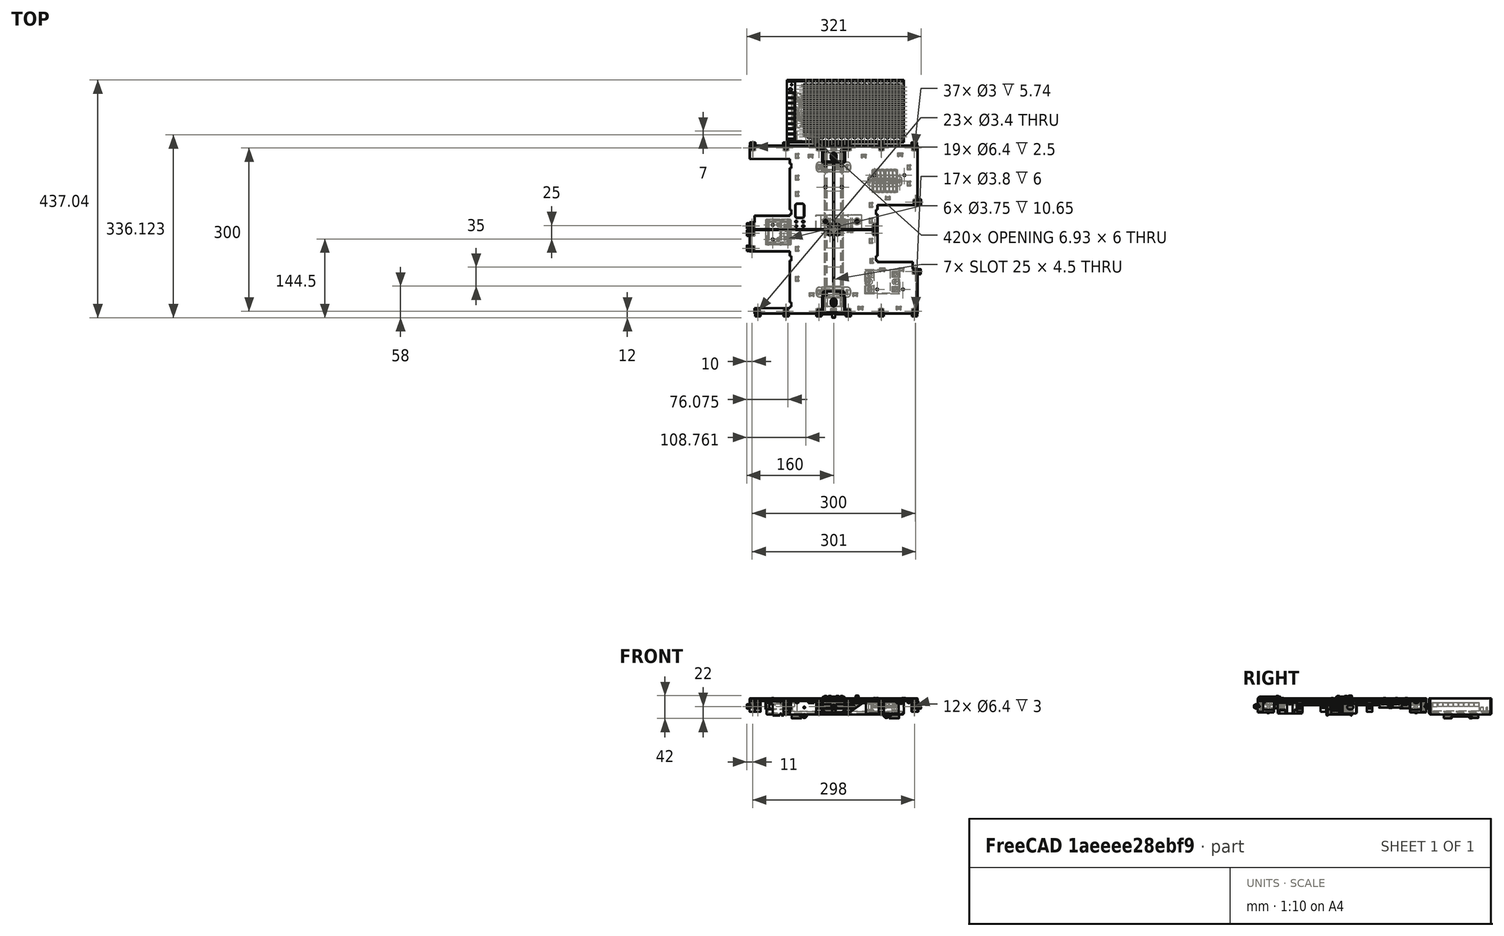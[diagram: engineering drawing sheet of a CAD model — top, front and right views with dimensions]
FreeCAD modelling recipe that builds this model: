
FCSTD DOCUMENT  (FreeCAD 0.19R24291 (Git))
Label: bottom-panel-assembly
License: Other
LicenseURL: GPL3
objects: Part::FeaturePython×86, Part::Feature×43, App::Part×10, PartDesign::CoordinateSystem×1
note: 130 computed .brp shape members not serialized (recipe doc carries the construction recipe); baked Part::Feature solids carry a one-line shape summary decoded from their .brp

FEATURE [Part::Feature] Cut002015026005020007004001  label="center-panel-connector"
  Placement = pos=(0,0,30) rot=(0,0,1;0rad)
  shape: bbox 22 x 22 x 3 mm, 24 faces (baked)
FEATURE [Part::FeaturePython] Screw013  label="M3x6-Screw"  # Fasteners workbench fastener (typed FeaturePython)
  Placement = pos=(-7,-7,33) rot=(0,0,1;0rad)
  baseObject = -> Cut002015026005020007004001 [Edge41]
  diameter = 1
  invert = false
  length = 0
  lengthCustom = 6
  matchOuter = true
  offset = 0
  thread = false
  type = 40
FEATURE [Part::FeaturePython] Screw014  label="M3x6-Screw014"  # Fasteners workbench fastener (typed FeaturePython)
  Placement = pos=(-7,7,33) rot=(0,0,1;0rad)
  baseObject = -> Cut002015026005020007004001 [Edge42]
  diameter = 1
  invert = false
  length = 0
  lengthCustom = 6
  matchOuter = true
  offset = 0
  thread = false
  type = 40
FEATURE [Part::FeaturePython] Screw015  label="M3x6-Screw015"  # Fasteners workbench fastener (typed FeaturePython)
  Placement = pos=(7,7,33) rot=(0,0,1;0rad)
  baseObject = -> Cut002015026005020007004001 [Edge40]
  diameter = 1
  invert = false
  length = 0
  lengthCustom = 6
  matchOuter = true
  offset = 0
  thread = false
  type = 40
FEATURE [Part::FeaturePython] Screw016  label="M3x6-Screw016"  # Fasteners workbench fastener (typed FeaturePython)
  Placement = pos=(7,-7,33) rot=(0,0,1;0rad)
  baseObject = -> Cut002015026005020007004001 [Edge39]
  diameter = 1
  invert = false
  length = 0
  lengthCustom = 6
  matchOuter = true
  offset = 0
  thread = false
  type = 40
FEATURE [Part::Feature] Cut001001  label="front-din-cap"
  Placement = pos=(0,-140,25) rot=(0,0,1;0rad)
  shape: bbox 40 x 41.5 x 9 mm, 50 faces (baked)
FEATURE [Part::Feature] Chamfer003004002  label="bottom-din-holder"
  Placement = pos=(-3.4e-14,-140,0) rot=(0,0,1;3.14159rad)
  shape: bbox 40 x 31 x 21 mm, 75 faces (baked)
FEATURE [Part::Feature] Chamfer005007002029002004001  label="back-din-cap"
  Placement = pos=(0,140,0) rot=(0,0,1;0rad)
  shape: bbox 40 x 30 x 6 mm, 55 faces (baked)
FEATURE [Part::Feature] Chamfer003001001  label="bottom-din-holder001"
  Placement = pos=(0,140,0) rot=(0,0,1;0rad)
  shape: bbox 40 x 31 x 21 mm, 75 faces (baked)
FEATURE [Part::Feature] Common001001  label="din-282mm001"
  Placement = pos=(-5e-15,0.5,24.5) rot=(0.707107,0.707107,0;3.14159rad)
  shape: bbox 35 x 282 x 7.5 mm, 66 faces (baked)
FEATURE [Part::FeaturePython] Nut  label="M4-Nut"  # Fasteners workbench fastener (typed FeaturePython)
  Placement = pos=(0,136,7) rot=(1,0,0;3.14159rad)
  baseObject = -> Chamfer003001001 [Edge141]
  diameter = 6
  invert = true
  matchOuter = true
  offset = 0
  thread = false
  type = 7
FEATURE [Part::FeaturePython] Nut001  label="M4-Nut001"  # Fasteners workbench fastener (typed FeaturePython)
  Placement = pos=(-3.4e-14,-136,7) rot=(1,0,0;3.14159rad)
  baseObject = -> Chamfer003004002 [Edge141]
  diameter = 6
  invert = true
  matchOuter = true
  offset = 0
  thread = false
  type = 7
FEATURE [Part::FeaturePython] HeatSet034  label="M3x4-HeatSet026"  # WARN: FeaturePython — macro-defined, semantics opaque (R4)
  Placement = pos=(-15,145,30) rot=(0,0,1;0rad)
  baseObject = -> Chamfer005007002029002004001 [Edge88]
  diameter = 2
  invert = false
  offset = 0
FEATURE [Part::FeaturePython] HeatSet035  label="M3x4-HeatSet027"  # WARN: FeaturePython — macro-defined, semantics opaque (R4)
  Placement = pos=(15,145,30) rot=(0,0,1;0rad)
  baseObject = -> Chamfer005007002029002004001 [Edge114]
  diameter = 2
  invert = false
  offset = 0
FEATURE [Part::FeaturePython] Screw034  label="M3x6-Screw019"  # Fasteners workbench fastener (typed FeaturePython)
  Placement = pos=(15,-119,33) rot=(0,0,1;0rad)
  baseObject = -> Cut001001 [Edge45]
  diameter = 1
  invert = false
  length = 0
  lengthCustom = 6
  matchOuter = true
  offset = 0
  thread = false
  type = 40
FEATURE [Part::FeaturePython] Screw035  label="M3x6-Screw020"  # Fasteners workbench fastener (typed FeaturePython)
  Placement = pos=(-15,-119,33) rot=(0,0,1;0rad)
  baseObject = -> Cut001001 [Edge44]
  diameter = 1
  invert = false
  length = 0
  lengthCustom = 6
  matchOuter = true
  offset = 0
  thread = false
  type = 40
FEATURE [Part::FeaturePython] Screw038  label="M6x12-Screw"  # Fasteners workbench fastener (typed FeaturePython)
  Placement = pos=(-3.4e-14,-150,15) rot=(-1,0,0;1.5708rad)
  baseObject = -> Chamfer003004002 [Edge49]
  diameter = 4
  invert = true
  length = 1
  lengthCustom = 12
  matchOuter = true
  offset = 0
  thread = false
  type = 40
FEATURE [Part::FeaturePython] Screw039  label="M6x12-Screw001"  # Fasteners workbench fastener (typed FeaturePython)
  Placement = pos=(0,150,15) rot=(1,0,0;1.5708rad)
  baseObject = -> Chamfer003001001 [Edge49]
  diameter = 4
  invert = true
  length = 1
  lengthCustom = 12
  matchOuter = true
  offset = 0
  thread = false
  type = 40
FEATURE [Part::FeaturePython] Screw040  label="M4x25-Screw"  # Fasteners workbench fastener (typed FeaturePython)
  Placement = pos=(2.6e-14,136,27.5) rot=(0,0,1;0rad)
  baseObject = -> Chamfer005007002029002004001 [Edge49]
  diameter = 2
  invert = false
  length = 7
  lengthCustom = 25
  matchOuter = true
  offset = 0
  thread = false
  type = 40
FEATURE [Part::FeaturePython] Screw041  label="M4x25-Screw001"  # Fasteners workbench fastener (typed FeaturePython)
  Placement = pos=(-3.4e-14,-136,27.5) rot=(0,0,1;0rad)
  baseObject = -> Cut001001 [Edge118]
  diameter = 2
  invert = false
  length = 7
  lengthCustom = 25
  matchOuter = true
  offset = 0
  thread = false
  type = 40
FEATURE [App::Part] Part002  label="din-mounter"
  Group = -> [Cut001001,Chamfer003004002,Chamfer005007002029002004001,Chamfer003001001,Common001001,Nut001,Nut,HeatSet034,HeatSet035,Screw034,Screw035,Screw038,Screw039,Screw040,Screw041]
  Origin = -> Origin002
FEATURE [Part::Feature] Cut002001001  label="sonoff-mount"
  Placement = pos=(-102,-4.75,24.5) rot=(0.707107,-0.707107,0;3.14159rad)
  shape: bbox 47 x 47 x 26.5 mm, 108 faces (baked)
FEATURE [Part::Feature] Fusion006002011004053036004001028003005004  label="SonOff-mini"
  Placement = pos=(-102,-5,10) rot=(0.57735,-0.57735,0.57735;4.18879rad)
  shape: bbox 43.4 x 42.65 x 19.85 mm, 152 faces (baked)
FEATURE [Part::Feature] Cut009001  label="wago-mount"
  Placement = pos=(95,89,24.5) rot=(0.707107,0.707107,0;3.14159rad)
  shape: bbox 63.6 x 41.99 x 12.2 mm, 224 faces (baked)
FEATURE [Part::Feature] Part__Feature001  label="WAGO 222-3c-002"
  Placement = pos=(71.5,89.5,22.5) rot=(0.57735,-0.57735,0.57735;4.18879rad)
  shape: bbox 22.7 x 21.3 x 9.8 mm, 151 faces (baked)
FEATURE [Part::Feature] Part__Feature003  label="WAGO 222-3c-004"
  Placement = pos=(94.2,89.5,22.5) rot=(0.57735,0.57735,-0.57735;4.18879rad)
  shape: bbox 22.7 x 21.3 x 9.8 mm, 151 faces (baked)
FEATURE [Part::Feature] Part__Feature002  label="WAGO 222-3c-003"
  Placement = pos=(116.7,89.5,22.5) rot=(0.57735,0.57735,-0.57735;4.18879rad)
  shape: bbox 22.7 x 21.3 x 9.8 mm, 151 faces (baked)
FEATURE [Part::Feature] Part__Feature  label="WAGO 222-3c-001"
  Placement = pos=(94,89.5,22.5) rot=(0.57735,-0.57735,0.57735;4.18879rad)
  shape: bbox 22.7 x 21.3 x 9.8 mm, 151 faces (baked)
FEATURE [Part::Feature] Fusion006002011004053036004001028003005005  label="SSR0omron"
  Placement = pos=(89,-96,2.5) rot=(0.57735,-0.57735,0.57735;4.18879rad)
  shape: bbox 64 x 45 x 22.5 mm, 84 faces (baked)
FEATURE [Part::FeaturePython] Screw042  label="M3x6-Screw021"  # Fasteners workbench fastener (typed FeaturePython)
  Placement = pos=(-102,-19,21.5) rot=(1,0,0;3.14159rad)
  baseObject = -> Cut002001001 [Edge319]
  diameter = 1
  invert = false
  length = 0
  lengthCustom = 6
  matchOuter = true
  offset = 0
  thread = false
  type = 40
FEATURE [Part::FeaturePython] Screw043  label="M3x6-Screw022"  # Fasteners workbench fastener (typed FeaturePython)
  Placement = pos=(-102,8.5,21.5) rot=(1,0,0;3.14159rad)
  baseObject = -> Cut002001001 [Edge316]
  diameter = 1
  invert = false
  length = 0
  lengthCustom = 6
  matchOuter = true
  offset = 0
  thread = false
  type = 40
FEATURE [App::Part] Part003  label="sonoff-switch"
  Group = -> [Fusion006002011004053036004001028003005004,Cut002001001,Screw042,Screw043]
  Origin = -> Origin003
  Placement = pos=(-10,0,0) rot=(0,0,1;0rad)
FEATURE [Part::FeaturePython] Screw044  label="M3x6-Screw024"  # Fasteners workbench fastener (typed FeaturePython)
  Placement = pos=(66.5,89,21.5) rot=(1,0,0;3.14159rad)
  baseObject = -> Cut009001 [Edge435]
  diameter = 1
  invert = false
  length = 0
  lengthCustom = 6
  matchOuter = true
  offset = 0
  thread = false
  type = 40
FEATURE [Part::FeaturePython] Screw045  label="M3x6-Screw023"  # Fasteners workbench fastener (typed FeaturePython)
  Placement = pos=(121.5,89,21.5) rot=(1,0,0;3.14159rad)
  baseObject = -> Cut009001 [Edge192]
  diameter = 1
  invert = false
  length = 0
  lengthCustom = 6
  matchOuter = true
  offset = 0
  thread = false
  type = 40
FEATURE [App::Part] Part004  label="wago-connectors"
  Group = -> [Screw045,Screw044,Part__Feature001,Part__Feature003,Part__Feature002,Part__Feature,Cut009001]
  Origin = -> Origin004
  Placement = pos=(8.5,11,0) rot=(0,0,1;0rad)
FEATURE [Part::FeaturePython] Washer001  label="M3-Washer"  # Fasteners workbench fastener (typed FeaturePython)
  Placement = pos=(113.418,-96,21.5) rot=(1,0,0;3.14159rad)
  baseObject = -> Fusion006002011004053036004001028003005005 [Edge76]
  diameter = 4
  invert = false
  matchOuter = true
  offset = 0
  type = 5
FEATURE [Part::FeaturePython] Washer  label="M3-Washer001"  # Fasteners workbench fastener (typed FeaturePython)
  Placement = pos=(65.4176,-96,21.5) rot=(1,0,0;3.14159rad)
  baseObject = -> Fusion006002011004053036004001028003005005 [Edge152]
  diameter = 4
  invert = false
  matchOuter = true
  offset = 0
  type = 5
FEATURE [Part::FeaturePython] Screw046  label="M3x6-Screw025"  # Fasteners workbench fastener (typed FeaturePython)
  Placement = pos=(65.4176,-96,20.95) rot=(1,0,0;3.14159rad)
  baseObject = -> Washer [Edge1]
  diameter = 1
  invert = false
  length = 0
  lengthCustom = 6
  matchOuter = true
  offset = 0
  thread = false
  type = 40
FEATURE [Part::FeaturePython] Screw047  label="M3x6-Screw026"  # Fasteners workbench fastener (typed FeaturePython)
  Placement = pos=(113.418,-96,20.95) rot=(1,0,0;3.14159rad)
  baseObject = -> Washer001 [Edge1]
  diameter = 1
  invert = false
  length = 0
  lengthCustom = 6
  matchOuter = true
  offset = 0
  thread = false
  type = 40
FEATURE [App::Part] Part005  label="ssr"
  Group = -> [Washer001,Washer,Screw046,Screw047,Fusion006002011004053036004001028003005005]
  Origin = -> Origin005
  Placement = pos=(14.5,-14,0) rot=(0,0,1;0rad)
FEATURE [Part::Feature] Fusion006002011004053036004001028003005014018035002002  label="lrs-psu"
  Placement = pos=(0,-5,0) rot=(0,0,1;0rad)
  shape: bbox 215 x 115 x 30.01 mm, 2625 faces, 2 solids (baked)
FEATURE [PartDesign::CoordinateSystem] LCS_bottom_panel_assembly  label="LCS_bottom-panel-assembly"
  AttacherType = Attacher::AttachEngine3D
FEATURE [Part::Feature] Cut026001  label="din-wire-mounter"
  Placement = pos=(-0.5,115,23.5) rot=(0.707107,0.707107,0;3.14159rad)
  shape: bbox 63.6 x 18 x 7.6 mm, 203 faces (baked)
FEATURE [Part::Feature] Cut002015026005020007014007002001002  label="din-wire-mounter001"
  Placement = pos=(-0.5,-115,23.5) rot=(0.707107,0.707107,0;3.14159rad)
  shape: bbox 63.6 x 18 x 7.6 mm, 203 faces (baked)
FEATURE [App::Part] Part008  label="extra-cable-mounter"
  Group = -> [Cut026001,Cut002015026005020007014007002001002]
  Origin = -> Origin008
FEATURE [Part::Feature] Part__Feature112001118  label="IEC Screw Mount Plug Socket Male"
  Placement = pos=(13,3e-15,14) rot=(0,0.707107,-0.707107;3.14159rad)
  shape: bbox 51.91 x 24.6 x 22.99 mm, 108 faces (baked)
FEATURE [Part::FeaturePython] Screw056  label="M6x25-Screw"  # Fasteners workbench fastener (typed FeaturePython)
  Placement = pos=(-15,15,8) rot=(1,0,0;3.14159rad)
  diameter = 4
  invert = true
  length = 5
  lengthCustom = 25
  matchOuter = true
  offset = 0
  thread = false
  type = 40
FEATURE [Part::FeaturePython] Screw057  label="M6x14-Screw"  # Fasteners workbench fastener (typed FeaturePython)
  Placement = pos=(43,15,21) rot=(1,0,0;3.14159rad)
  diameter = 4
  invert = true
  length = 2
  lengthCustom = 14
  matchOuter = true
  offset = 0
  thread = false
  type = 40
FEATURE [Part::FeaturePython] HeatSet040  label="M3x4-HeatSet033"  # WARN: FeaturePython — macro-defined, semantics opaque (R4)
  Placement = pos=(-7,4e-15,14) rot=(1,0,0;1.5708rad)
  diameter = 2
  invert = true
  offset = 0
FEATURE [Part::FeaturePython] HeatSet041  label="M3x4-HeatSet032"  # WARN: FeaturePython — macro-defined, semantics opaque (R4)
  Placement = pos=(33,4e-15,14) rot=(1,0,0;1.5708rad)
  diameter = 2
  invert = true
  offset = 0
FEATURE [Part::FeaturePython] Screw058  label="M3x10-Screw036"  # Fasteners workbench fastener (typed FeaturePython)
  Placement = pos=(-7,-2.5,14) rot=(1,0,0;1.5708rad)
  baseObject = -> Part__Feature112001118 [Edge8]
  diameter = 4
  invert = false
  length = 3
  lengthCustom = 10
  matchOuter = true
  offset = 1
  thread = false
  type = 34
FEATURE [Part::FeaturePython] Screw059  label="M3x10-Screw035"  # Fasteners workbench fastener (typed FeaturePython)
  Placement = pos=(33,-2.5,14) rot=(1,0,0;1.5708rad)
  baseObject = -> Part__Feature112001118 [Edge12]
  diameter = 4
  invert = false
  length = 3
  lengthCustom = 10
  matchOuter = true
  offset = 1
  thread = false
  type = 34
FEATURE [Part::Feature] Chamfer005007002028001  label="panel-FR"
  Placement = pos=(0,0,25) rot=(0,0,1;0rad)
  shape: bbox 154 x 154 x 9 mm, 176 faces (baked)
FEATURE [Part::Feature] Chamfer005007002028002  label="panel-BR"
  Placement = pos=(0,0,25) rot=(0,0,1;0rad)
  shape: bbox 154 x 154 x 9 mm, 173 faces (baked)
FEATURE [Part::Feature] Chamfer005007002027001  label="panel-FL"
  Placement = pos=(0,0,25) rot=(0,0,1;0rad)
  shape: bbox 154 x 154 x 9 mm, 125 faces (baked)
FEATURE [Part::FeaturePython] HeatSet  label="M3x4-HeatSet"  # WARN: FeaturePython — macro-defined, semantics opaque (R4)
  Placement = pos=(15,118,25) rot=(1,0,0;3.14159rad)
  baseObject = -> Chamfer005007002028002 [Edge77]
  diameter = 2
  invert = true
  offset = 0
FEATURE [Part::Feature] Chamfer005007002030001  label="panel-BL"
  Placement = pos=(0,0,25) rot=(0,0,1;0rad)
  shape: bbox 154 x 154 x 9 mm, 202 faces (baked)
FEATURE [Part::FeaturePython] HeatSet042  label="M3x4-HeatSet034"  # WARN: FeaturePython — macro-defined, semantics opaque (R4)
  Placement = pos=(-15,118,25) rot=(1,0,0;3.14159rad)
  baseObject = -> Chamfer005007002030001 [Edge68]
  diameter = 2
  invert = true
  offset = 0
FEATURE [Part::FeaturePython] HeatSet043  label="M3x4-HeatSet035"  # WARN: FeaturePython — macro-defined, semantics opaque (R4)
  Placement = pos=(-15,78,25) rot=(1,0,0;3.14159rad)
  baseObject = -> Chamfer005007002030001 [Edge67]
  diameter = 2
  invert = true
  offset = 0
FEATURE [Part::FeaturePython] HeatSet044  label="M3x4-HeatSet036"  # WARN: FeaturePython — macro-defined, semantics opaque (R4)
  Placement = pos=(-7,7,25) rot=(1,0,0;3.14159rad)
  baseObject = -> Chamfer005007002030001 [Edge66]
  diameter = 2
  invert = true
  offset = 0
FEATURE [Part::FeaturePython] HeatSet045  label="M3x4-HeatSet037"  # WARN: FeaturePython — macro-defined, semantics opaque (R4)
  Placement = pos=(15,78,25) rot=(1,0,0;3.14159rad)
  baseObject = -> Chamfer005007002028002 [Edge75]
  diameter = 2
  invert = true
  offset = 0
FEATURE [Part::FeaturePython] HeatSet046  label="M3x4-HeatSet038"  # WARN: FeaturePython — macro-defined, semantics opaque (R4)
  Placement = pos=(7,7,25) rot=(1,0,0;3.14159rad)
  baseObject = -> Chamfer005007002028002 [Edge74]
  diameter = 2
  invert = true
  offset = 0
FEATURE [Part::FeaturePython] HeatSet047  label="M3x4-HeatSet039"  # WARN: FeaturePython — macro-defined, semantics opaque (R4)
  Placement = pos=(-7,-7,25) rot=(1,0,0;3.14159rad)
  baseObject = -> Chamfer005007002027001 [Edge170]
  diameter = 2
  invert = true
  offset = 0
FEATURE [Part::FeaturePython] HeatSet048  label="M3x4-HeatSet040"  # WARN: FeaturePython — macro-defined, semantics opaque (R4)
  Placement = pos=(-15,-119,25) rot=(1,0,0;3.14159rad)
  baseObject = -> Chamfer005007002027001 [Edge168]
  diameter = 2
  invert = true
  offset = 0
FEATURE [Part::FeaturePython] HeatSet049  label="M3x4-HeatSet041"  # WARN: FeaturePython — macro-defined, semantics opaque (R4)
  Placement = pos=(7,-7,25) rot=(1,0,0;3.14159rad)
  baseObject = -> Chamfer005007002028001 [Edge79]
  diameter = 2
  invert = true
  offset = 0
FEATURE [Part::FeaturePython] HeatSet050  label="M3x4-HeatSet042"  # WARN: FeaturePython — macro-defined, semantics opaque (R4)
  Placement = pos=(15,-119,25) rot=(1,0,0;3.14159rad)
  baseObject = -> Chamfer005007002028001 [Edge76]
  diameter = 2
  invert = true
  offset = 0
FEATURE [Part::FeaturePython] HeatSet051  label="M3x3-HeatSet"  # WARN: FeaturePython — macro-defined, semantics opaque (R4)
  Placement = pos=(-112,-18,25) rot=(1,0,0;3.14159rad)
  baseObject = -> Chamfer005007002027001 [Edge195]
  diameter = 2
  invert = true
  offset = 0
FEATURE [Part::FeaturePython] HeatSet052  label="M3x3-HeatSet001"  # WARN: FeaturePython — macro-defined, semantics opaque (R4)
  Placement = pos=(-112,8.5,25) rot=(1,0,0;3.14159rad)
  baseObject = -> Chamfer005007002030001 [Edge65]
  diameter = 2
  invert = true
  offset = 0
FEATURE [Part::FeaturePython] HeatSet053  label="M3x3-HeatSet002"  # WARN: FeaturePython — macro-defined, semantics opaque (R4)
  Placement = pos=(80,-110,25) rot=(1,0,0;3.14159rad)
  baseObject = -> Chamfer005007002028001 [Edge77]
  diameter = 2
  invert = true
  offset = 0
FEATURE [Part::FeaturePython] HeatSet054  label="M3x3-HeatSet003"  # WARN: FeaturePython — macro-defined, semantics opaque (R4)
  Placement = pos=(127.5,-110,25) rot=(1,0,0;3.14159rad)
  baseObject = -> Chamfer005007002028001 [Edge78]
  diameter = 2
  invert = true
  offset = 0
FEATURE [Part::FeaturePython] HeatSet055  label="M3x3-HeatSet004"  # WARN: FeaturePython — macro-defined, semantics opaque (R4)
  Placement = pos=(75,100,25) rot=(1,0,0;3.14159rad)
  baseObject = -> Chamfer005007002028002 [Edge76]
  diameter = 2
  invert = true
  offset = 0
FEATURE [Part::FeaturePython] HeatSet056  label="M3x3-HeatSet005"  # WARN: FeaturePython — macro-defined, semantics opaque (R4)
  Placement = pos=(130,100,25) rot=(1,0,0;3.14159rad)
  baseObject = -> Chamfer005007002028002 [Edge78]
  diameter = 2
  invert = true
  offset = 0
FEATURE [Part::Feature] Pocket003011  label="panel-mounter_U001"
  Placement = pos=(-144,155,15) rot=(0.57735,-0.57735,-0.57735;2.0944rad)
  shape: bbox 10 x 15 x 20 mm, 54 faces (baked)
FEATURE [Part::Feature] Chamfer001  label="panel-side-connector"
  Placement = pos=(76,0,20) rot=(0,0,1;0rad)
  shape: bbox 10 x 23 x 5 mm, 32 faces (baked)
FEATURE [Part::FeaturePython] HeatSet057  label="M3x4-HeatSet043"  # WARN: FeaturePython — macro-defined, semantics opaque (R4)
  Placement = pos=(76,-6.5,20) rot=(1,0,0;3.14159rad)
  baseObject = -> Chamfer001 [Edge30]
  diameter = 2
  invert = true
  offset = 0
FEATURE [Part::FeaturePython] HeatSet058  label="M3x4-HeatSet001"  # WARN: FeaturePython — macro-defined, semantics opaque (R4)
  Placement = pos=(76,6.5,20) rot=(1,0,0;3.14159rad)
  baseObject = -> Chamfer001 [Edge31]
  diameter = 2
  invert = true
  offset = 0
FEATURE [Part::FeaturePython] Screw  label="M3x6-Screw027"  # Fasteners workbench fastener (typed FeaturePython)
  Placement = pos=(148.5,150,27.5) rot=(0,0,1;0rad)
  baseObject = -> Chamfer005007002028002 [Edge251]
  diameter = 1
  invert = false
  length = 0
  lengthCustom = 6
  matchOuter = true
  offset = 0
  thread = false
  type = 40
FEATURE [Part::FeaturePython] Screw060  label="M3x6-Screw028"  # Fasteners workbench fastener (typed FeaturePython)
  Placement = pos=(150,50.64,27.5) rot=(0,0,1;0rad)
  baseObject = -> Chamfer005007002028002 [Edge165]
  diameter = 1
  invert = false
  length = 0
  lengthCustom = 6
  matchOuter = true
  offset = 0
  thread = false
  type = 40
FEATURE [Part::FeaturePython] Screw061  label="M3x6-Screw029"  # Fasteners workbench fastener (typed FeaturePython)
  Placement = pos=(87.75,150,27.5) rot=(0,0,1;0rad)
  baseObject = -> Chamfer005007002028002 [Edge209]
  diameter = 1
  invert = false
  length = 0
  lengthCustom = 6
  matchOuter = true
  offset = 0
  thread = false
  type = 40
FEATURE [Part::FeaturePython] Screw062  label="M3x6-Screw030"  # Fasteners workbench fastener (typed FeaturePython)
  Placement = pos=(27,150,27.5) rot=(0,0,1;0rad)
  baseObject = -> Chamfer005007002028002 [Edge167]
  diameter = 1
  invert = false
  length = 0
  lengthCustom = 6
  matchOuter = true
  offset = 0
  thread = false
  type = 40
FEATURE [Part::FeaturePython] Screw063  label="M3x6-Screw031"  # Fasteners workbench fastener (typed FeaturePython)
  Placement = pos=(-27,150,27.5) rot=(0,0,1;0rad)
  baseObject = -> Chamfer005007002030001 [Edge247]
  diameter = 1
  invert = false
  length = 0
  lengthCustom = 6
  matchOuter = true
  offset = 0
  thread = false
  type = 40
FEATURE [Part::FeaturePython] Screw064  label="M3x6-Screw032"  # Fasteners workbench fastener (typed FeaturePython)
  Placement = pos=(-87.75,150,27.5) rot=(0,0,1;0rad)
  baseObject = -> Chamfer005007002030001 [Edge185]
  diameter = 1
  invert = false
  length = 0
  lengthCustom = 6
  matchOuter = true
  offset = 0
  thread = false
  type = 40
FEATURE [Part::FeaturePython] Screw065  label="M3x6-Screw033"  # Fasteners workbench fastener (typed FeaturePython)
  Placement = pos=(-148.5,150,27.5) rot=(0,0,1;0rad)
  baseObject = -> Chamfer005007002030001 [Edge183]
  diameter = 1
  invert = false
  length = 0
  lengthCustom = 6
  matchOuter = true
  offset = 0
  thread = false
  type = 40
FEATURE [Part::FeaturePython] Screw066  label="M3x6-Screw034"  # Fasteners workbench fastener (typed FeaturePython)
  Placement = pos=(-150,6.5,27.5) rot=(0,0,1;0rad)
  baseObject = -> Chamfer005007002030001 [Edge161]
  diameter = 1
  invert = false
  length = 0
  lengthCustom = 6
  matchOuter = true
  offset = 0
  thread = false
  type = 40
FEATURE [Part::FeaturePython] Screw067  label="M3x6-Screw035"  # Fasteners workbench fastener (typed FeaturePython)
  Placement = pos=(-150,-6.5,27.5) rot=(0,0,1;0rad)
  baseObject = -> Chamfer005007002027001 [Edge116]
  diameter = 1
  invert = false
  length = 0
  lengthCustom = 6
  matchOuter = true
  offset = 0
  thread = false
  type = 40
FEATURE [Part::FeaturePython] Screw068  label="M3x6-Screw036"  # Fasteners workbench fastener (typed FeaturePython)
  Placement = pos=(-150,-34.36,27.5) rot=(0,0,1;0rad)
  baseObject = -> Chamfer005007002027001 [Edge115]
  diameter = 1
  invert = false
  length = 0
  lengthCustom = 6
  matchOuter = true
  offset = 0
  thread = false
  type = 40
FEATURE [Part::FeaturePython] Screw069  label="M3x6-Screw037"  # Fasteners workbench fastener (typed FeaturePython)
  Placement = pos=(-139.5,-150,27.5) rot=(0,0,1;0rad)
  baseObject = -> Chamfer005007002027001 [Edge112]
  diameter = 1
  invert = false
  length = 0
  lengthCustom = 6
  matchOuter = true
  offset = 0
  thread = false
  type = 40
FEATURE [Part::FeaturePython] Screw070  label="M3x6-Screw038"  # Fasteners workbench fastener (typed FeaturePython)
  Placement = pos=(-87.75,-150,27.5) rot=(0,0,1;0rad)
  baseObject = -> Chamfer005007002027001 [Edge113]
  diameter = 1
  invert = false
  length = 0
  lengthCustom = 6
  matchOuter = true
  offset = 0
  thread = false
  type = 40
FEATURE [Part::FeaturePython] Screw071  label="M3x6-Screw039"  # Fasteners workbench fastener (typed FeaturePython)
  Placement = pos=(-27,-150,27.5) rot=(0,0,1;0rad)
  baseObject = -> Chamfer005007002027001 [Edge114]
  diameter = 1
  invert = false
  length = 0
  lengthCustom = 6
  matchOuter = true
  offset = 0
  thread = false
  type = 40
FEATURE [Part::FeaturePython] Screw072  label="M3x6-Screw040"  # Fasteners workbench fastener (typed FeaturePython)
  Placement = pos=(27,-150,27.5) rot=(0,0,1;0rad)
  baseObject = -> Chamfer005007002028001 [Edge108]
  diameter = 1
  invert = false
  length = 0
  lengthCustom = 6
  matchOuter = true
  offset = 0
  thread = false
  type = 40
FEATURE [Part::FeaturePython] Screw073  label="M3x6-Screw041"  # Fasteners workbench fastener (typed FeaturePython)
  Placement = pos=(87.75,-150,27.5) rot=(0,0,1;0rad)
  baseObject = -> Chamfer005007002028001 [Edge150]
  diameter = 1
  invert = false
  length = 0
  lengthCustom = 6
  matchOuter = true
  offset = 0
  thread = false
  type = 40
FEATURE [Part::FeaturePython] Screw074  label="M3x6-Screw042"  # Fasteners workbench fastener (typed FeaturePython)
  Placement = pos=(148.5,-150,27.5) rot=(0,0,1;0rad)
  baseObject = -> Chamfer005007002028001 [Edge172]
  diameter = 1
  invert = false
  length = 0
  lengthCustom = 6
  matchOuter = true
  offset = 0
  thread = false
  type = 40
FEATURE [Part::FeaturePython] Screw075  label="M3x6-Screw043"  # Fasteners workbench fastener (typed FeaturePython)
  Placement = pos=(76,6.5,27.5) rot=(0,0,1;0rad)
  baseObject = -> Chamfer005007002028002 [Edge143]
  diameter = 1
  invert = false
  length = 0
  lengthCustom = 6
  matchOuter = true
  offset = 0
  thread = false
  type = 40
FEATURE [Part::FeaturePython] Screw076  label="M3x6-Screw044"  # Fasteners workbench fastener (typed FeaturePython)
  Placement = pos=(76,-6.5,27.5) rot=(0,0,1;0rad)
  baseObject = -> Chamfer005007002028001 [Edge256]
  diameter = 1
  invert = false
  length = 0
  lengthCustom = 6
  matchOuter = true
  offset = 0
  thread = false
  type = 40
FEATURE [Part::Feature] Pocket003012  label="panel-mounter_U002"
  Placement = pos=(-83,155,15) rot=(0.57735,-0.57735,-0.57735;2.0944rad)
  shape: bbox 10 x 15 x 20 mm, 54 faces (baked)
FEATURE [Part::Feature] Pocket003013  label="panel-mounter_U003"
  Placement = pos=(-22,155,15) rot=(0.57735,-0.57735,-0.57735;2.0944rad)
  shape: bbox 10 x 15 x 20 mm, 54 faces (baked)
FEATURE [Part::Feature] Pocket003014  label="panel-mounter_U004"
  Placement = pos=(32,155,15) rot=(0.57735,-0.57735,-0.57735;2.0944rad)
  shape: bbox 10 x 15 x 20 mm, 54 faces (baked)
FEATURE [Part::Feature] Pocket003015  label="panel-mounter_U005"
  Placement = pos=(92.5,155,15) rot=(0.57735,-0.57735,-0.57735;2.0944rad)
  shape: bbox 10 x 15 x 20 mm, 54 faces (baked)
FEATURE [Part::Feature] Pocket003016  label="panel-mounter_U006"
  Placement = pos=(153,155,15) rot=(0.57735,-0.57735,-0.57735;2.0944rad)
  shape: bbox 10 x 15 x 20 mm, 54 faces (baked)
FEATURE [Part::Feature] Pocket003017  label="panel-mounter_U007"
  Placement = pos=(156,45.5,15) rot=(0,0.707107,0.707107;3.14159rad)
  shape: bbox 15 x 10 x 20 mm, 54 faces (baked)
FEATURE [Part::Feature] Pocket003018  label="panel-mounter_U008"
  Placement = pos=(155,-82.5,15) rot=(0,0.707107,0.707107;3.14159rad)
  shape: bbox 15 x 10 x 20 mm, 54 faces (baked)
FEATURE [Part::Feature] Pocket003019  label="panel-mounter_U009"
  Placement = pos=(144,-155,15) rot=(0.57735,0.57735,0.57735;2.0944rad)
  shape: bbox 10 x 15 x 20 mm, 54 faces (baked)
FEATURE [Part::Feature] Pocket003020  label="panel-mounter_U010"
  Placement = pos=(82.5,-155,15) rot=(0.57735,0.57735,0.57735;2.0944rad)
  shape: bbox 10 x 15 x 20 mm, 54 faces (baked)
FEATURE [Part::Feature] Pocket003021  label="panel-mounter_U011"
  Placement = pos=(22,-155,15) rot=(0.57735,0.57735,0.57735;2.0944rad)
  shape: bbox 10 x 15 x 20 mm, 54 faces (baked)
FEATURE [Part::Feature] Pocket003022  label="panel-mounter_U012"
  Placement = pos=(-32,-155,15) rot=(0.57735,0.57735,0.57735;2.0944rad)
  shape: bbox 10 x 15 x 20 mm, 54 faces (baked)
FEATURE [Part::Feature] Pocket003023  label="panel-mounter_U013"
  Placement = pos=(-92.5,-155,15) rot=(0.57735,0.57735,0.57735;2.0944rad)
  shape: bbox 10 x 15 x 20 mm, 54 faces (baked)
FEATURE [Part::Feature] Pocket003024  label="panel-mounter_U014"
  Placement = pos=(-144.5,-155,15) rot=(0.57735,0.57735,0.57735;2.0944rad)
  shape: bbox 10 x 15 x 20 mm, 54 faces (baked)
FEATURE [Part::Feature] Pocket003025  label="panel-mounter_U015"
  Placement = pos=(-155,-29.5,15) rot=(1,0,0;1.5708rad)
  shape: bbox 15 x 10 x 20 mm, 54 faces (baked)
FEATURE [Part::Feature] Pocket003026  label="panel-mounter_U016"
  Placement = pos=(-155,-1.5,15) rot=(1,0,0;1.5708rad)
  shape: bbox 15 x 10 x 20 mm, 54 faces (baked)
FEATURE [Part::Feature] Pocket003027  label="panel-mounter_U017"
  Placement = pos=(-155,11.5,15) rot=(1,0,0;1.5708rad)
  shape: bbox 15 x 10 x 20 mm, 54 faces (baked)
FEATURE [Part::FeaturePython] Screw077  label="M3x6-Screw045"  # Fasteners workbench fastener (typed FeaturePython)
  Placement = pos=(150,-77.5,27.5) rot=(0,0,1;0rad)
  baseObject = -> Chamfer005007002028001 [Edge174]
  diameter = 1
  invert = false
  length = 0
  lengthCustom = 6
  matchOuter = true
  offset = 0
  thread = false
  type = 40
FEATURE [App::Part] Part001  label="bottom-panel-plate"
  Group = -> [Cut002015026005020007004001,Screw013,Screw014,Screw015,Screw016,Chamfer005007002028001,Chamfer005007002028002,Chamfer005007002027001,Chamfer005007002030001,HeatSet,HeatSet042,HeatSet043,HeatSet044,HeatSet045,HeatSet046,HeatSet047,HeatSet048,HeatSet049,HeatSet050,HeatSet051,HeatSet052,HeatSet053,HeatSet054,HeatSet055,HeatSet056,Chamfer001,HeatSet057,HeatSet058,Screw060,Screw061,Screw062,Screw063,+15 more]
  Origin = -> Origin001
FEATURE [Part::FeaturePython] HeatSet059  label="M3x4-HeatSet044"  # WARN: FeaturePython — macro-defined, semantics opaque (R4)
  Placement = pos=(-149,150,25) rot=(0,0,1;0rad)
  baseObject = -> Pocket003011 [Edge44]
  diameter = 2
  invert = false
  offset = 0
FEATURE [Part::FeaturePython] HeatSet060  label="M3x4-HeatSet045"  # WARN: FeaturePython — macro-defined, semantics opaque (R4)
  Placement = pos=(-88,150,25) rot=(0,0,1;0rad)
  baseObject = -> Pocket003012 [Edge44]
  diameter = 2
  invert = false
  offset = 0
FEATURE [Part::FeaturePython] HeatSet061  label="M3x4-HeatSet046"  # WARN: FeaturePython — macro-defined, semantics opaque (R4)
  Placement = pos=(-27,150,25) rot=(0,0,1;0rad)
  baseObject = -> Pocket003013 [Edge44]
  diameter = 2
  invert = false
  offset = 0
FEATURE [Part::FeaturePython] HeatSet062  label="M3x4-HeatSet047"  # WARN: FeaturePython — macro-defined, semantics opaque (R4)
  Placement = pos=(27,150,25) rot=(0,0,1;0rad)
  baseObject = -> Pocket003014 [Edge44]
  diameter = 2
  invert = false
  offset = 0
FEATURE [Part::FeaturePython] HeatSet063  label="M3x4-HeatSet048"  # WARN: FeaturePython — macro-defined, semantics opaque (R4)
  Placement = pos=(87.5,150,25) rot=(0,0,1;0rad)
  baseObject = -> Pocket003015 [Edge44]
  diameter = 2
  invert = false
  offset = 0
FEATURE [Part::FeaturePython] HeatSet064  label="M3x4-HeatSet049"  # WARN: FeaturePython — macro-defined, semantics opaque (R4)
  Placement = pos=(148,150,25) rot=(0,0,1;0rad)
  baseObject = -> Pocket003016 [Edge44]
  diameter = 2
  invert = false
  offset = 0
FEATURE [Part::FeaturePython] HeatSet065  label="M3x4-HeatSet050"  # WARN: FeaturePython — macro-defined, semantics opaque (R4)
  Placement = pos=(151,50.5,25) rot=(0,0,1;0rad)
  baseObject = -> Pocket003017 [Edge44]
  diameter = 2
  invert = false
  offset = 0
FEATURE [Part::FeaturePython] HeatSet066  label="M3x4-HeatSet051"  # WARN: FeaturePython — macro-defined, semantics opaque (R4)
  Placement = pos=(150,-77.5,25) rot=(0,0,1;0rad)
  baseObject = -> Pocket003018 [Edge44]
  diameter = 2
  invert = false
  offset = 0
FEATURE [Part::FeaturePython] HeatSet067  label="M3x4-HeatSet052"  # WARN: FeaturePython — macro-defined, semantics opaque (R4)
  Placement = pos=(149,-150,25) rot=(0,0,1;0rad)
  baseObject = -> Pocket003019 [Edge44]
  diameter = 2
  invert = false
  offset = 0
FEATURE [Part::FeaturePython] HeatSet068  label="M3x4-HeatSet053"  # WARN: FeaturePython — macro-defined, semantics opaque (R4)
  Placement = pos=(87.5,-150,25) rot=(0,0,1;0rad)
  baseObject = -> Pocket003020 [Edge44]
  diameter = 2
  invert = false
  offset = 0
FEATURE [Part::FeaturePython] HeatSet069  label="M3x4-HeatSet054"  # WARN: FeaturePython — macro-defined, semantics opaque (R4)
  Placement = pos=(27,-150,25) rot=(0,0,1;0rad)
  baseObject = -> Pocket003021 [Edge44]
  diameter = 2
  invert = false
  offset = 0
FEATURE [Part::FeaturePython] HeatSet070  label="M3x4-HeatSet055"  # WARN: FeaturePython — macro-defined, semantics opaque (R4)
  Placement = pos=(-27,-150,25) rot=(0,0,1;0rad)
  baseObject = -> Pocket003022 [Edge44]
  diameter = 2
  invert = false
  offset = 0
FEATURE [Part::FeaturePython] HeatSet071  label="M3x4-HeatSet056"  # WARN: FeaturePython — macro-defined, semantics opaque (R4)
  Placement = pos=(-87.5,-150,25) rot=(0,0,1;0rad)
  baseObject = -> Pocket003023 [Edge44]
  diameter = 2
  invert = false
  offset = 0
FEATURE [Part::FeaturePython] HeatSet072  label="M3x4-HeatSet057"  # WARN: FeaturePython — macro-defined, semantics opaque (R4)
  Placement = pos=(-139.5,-150,25) rot=(0,0,1;0rad)
  baseObject = -> Pocket003024 [Edge44]
  diameter = 2
  invert = false
  offset = 0
FEATURE [Part::FeaturePython] HeatSet073  label="M3x4-HeatSet058"  # WARN: FeaturePython — macro-defined, semantics opaque (R4)
  Placement = pos=(-150,-34.5,25) rot=(0,0,1;0rad)
  baseObject = -> Pocket003025 [Edge44]
  diameter = 2
  invert = false
  offset = 0
FEATURE [Part::FeaturePython] HeatSet074  label="M3x4-HeatSet059"  # WARN: FeaturePython — macro-defined, semantics opaque (R4)
  Placement = pos=(-150,-6.5,25) rot=(0,0,1;0rad)
  baseObject = -> Pocket003026 [Edge44]
  diameter = 2
  invert = false
  offset = 0
FEATURE [Part::FeaturePython] HeatSet075  label="M3x4-HeatSet060"  # WARN: FeaturePython — macro-defined, semantics opaque (R4)
  Placement = pos=(-150,6.5,25) rot=(0,0,1;0rad)
  baseObject = -> Pocket003027 [Edge44]
  diameter = 2
  invert = false
  offset = 0
FEATURE [App::Part] Part  label="panel-mounter"
  Group = -> [Pocket003011,Pocket003012,Pocket003013,Pocket003014,Pocket003015,Pocket003016,Pocket003017,Pocket003018,Pocket003019,Pocket003020,Pocket003021,Pocket003022,Pocket003023,Pocket003024,Pocket003025,Pocket003026,Pocket003027,HeatSet059,HeatSet060,HeatSet061,HeatSet062,HeatSet063,HeatSet064,HeatSet065,HeatSet066,HeatSet067,HeatSet068,HeatSet069,HeatSet070,HeatSet071,HeatSet072,HeatSet073,HeatSet074,+1 more]
  Origin = -> Origin
FEATURE [Part::Feature] Part__Mirroring001  label="lrs-xx-200-psu-mounter-mirror"
  Placement = pos=(-68,218,-4) rot=(1,0,0;3.14159rad)
  shape: bbox 28 x 63.6 x 7.6 mm, 179 faces (baked)
FEATURE [Part::Feature] Fusion017004001001  label="lrs-xx-200-psu-mounter"
  Placement = pos=(111,218,-4) rot=(1,0,0;3.14159rad)
  shape: bbox 28 x 63.6 x 7.6 mm, 179 faces (baked)
FEATURE [Part::FeaturePython] Screw078  label="M4x6-Screw"  # Fasteners workbench fastener (typed FeaturePython)
  Placement = pos=(-54,243,-4) rot=(-0.225347,0.974279,0;3.14159rad)
  baseObject = -> Part__Mirroring001 [Edge394]
  diameter = 2
  invert = false
  length = 0
  lengthCustom = 6
  matchOuter = true
  offset = 0
  thread = false
  type = 40
FEATURE [Part::FeaturePython] Screw079  label="M4x6-Screw001"  # Fasteners workbench fastener (typed FeaturePython)
  Placement = pos=(-54,193,-4) rot=(-0.225347,0.974279,0;3.14159rad)
  baseObject = -> Part__Mirroring001 [Edge368]
  diameter = 2
  invert = false
  length = 0
  lengthCustom = 6
  matchOuter = true
  offset = 0
  thread = false
  type = 40
FEATURE [Part::FeaturePython] Screw080  label="M4x6-Screw004"  # Fasteners workbench fastener (typed FeaturePython)
  Placement = pos=(97,193,-4) rot=(1,0,0;3.14159rad)
  baseObject = -> Fusion017004001001 [Edge368]
  diameter = 2
  invert = true
  length = 0
  lengthCustom = 6
  matchOuter = true
  offset = 0
  thread = false
  type = 40
FEATURE [Part::FeaturePython] Screw081  label="M4x6-Screw005"  # Fasteners workbench fastener (typed FeaturePython)
  Placement = pos=(97,243,-4) rot=(1,0,0;3.14159rad)
  baseObject = -> Fusion017004001001 [Edge394]
  diameter = 2
  invert = true
  length = 0
  lengthCustom = 6
  matchOuter = true
  offset = 0
  thread = false
  type = 40
FEATURE [App::Part] Part006  label="psu-24v"
  Group = -> [Fusion006002011004053036004001028003005014018035002002,Fusion017004001001,Part__Mirroring001,Screw078,Screw079,Screw080,Screw081]
  Origin = -> Origin006
  Placement = pos=(218,21,12) rot=(-0.707107,0.707107,0;3.14159rad)
FEATURE [Part::Feature] Cut008004003004014002002008002001001  label="ac-socket-mounter001"
  shape: bbox 85 x 27 x 25 mm, 57 faces (baked)
FEATURE [App::Part] Part009  label="ac-connector"
  Group = -> [Part__Feature112001118,Screw056,Screw057,HeatSet041,HeatSet040,Screw059,Screw058,Cut008004003004014002002008002001001]
  Origin = -> Origin009
  Placement = pos=(122,183.5,-26) rot=(0,0,1;3.14159rad)
FEATURE [App::Part] Part007  label="bottom-panel"
  Group = -> [Part001,Part002,Part003,Part004,Part005,Part006,LCS_bottom_panel_assembly,Part008,Part009,Part]
  Origin = -> Origin007
